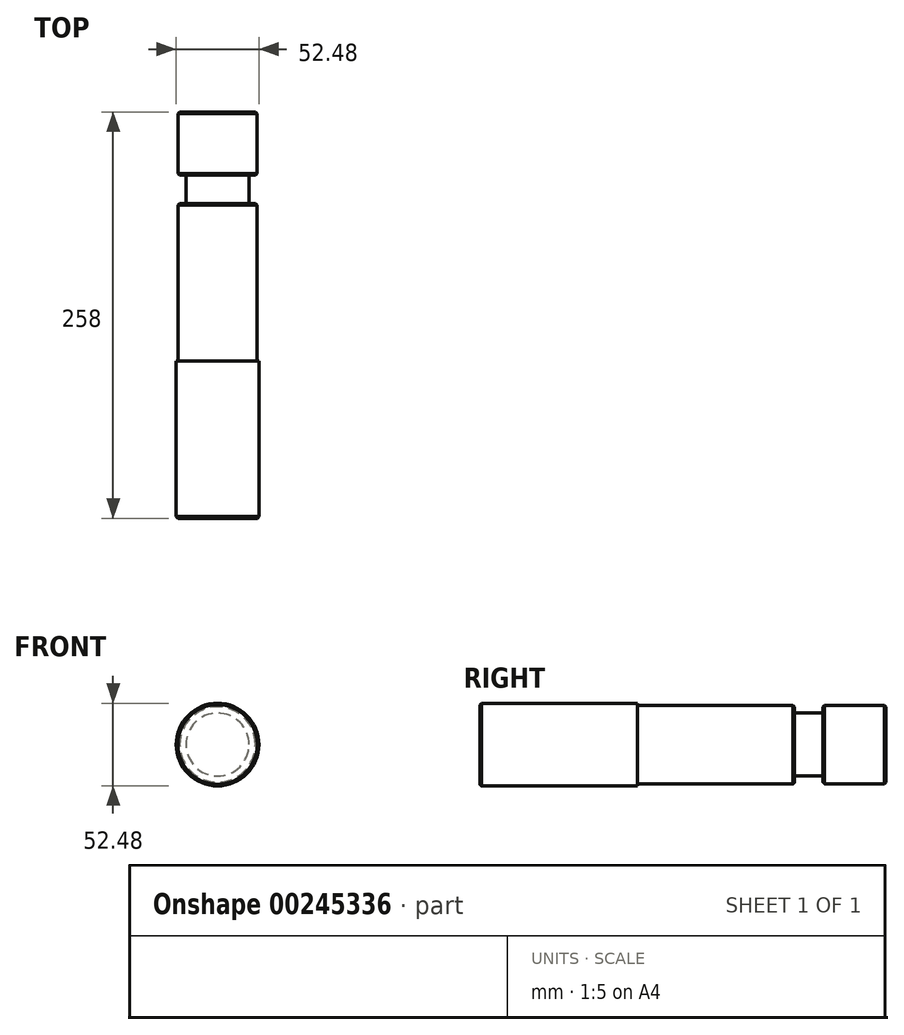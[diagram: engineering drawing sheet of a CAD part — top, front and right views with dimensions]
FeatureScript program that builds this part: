
annotation { "Feature Type Name" : "Feature", "Feature Type Description" : "" }
export const myFeature = defineFeature(function(context is Context, id is Id, definition is map)
    precondition{}
    {
        {
            var Q0;
            Q0=qCreatedBy(makeId("Front.planeOp"),FACE);
            var sketch = newSketch(context, id + "F0", { "sketchPlane" : qUnion([Q0])});
            skCircle(sketch, "E0", {"center": v(0, 0) * mm, "radius": 25 * mm});
            skSolve(sketch);
        }
        {
            var Q0;
            Q0 = qSketchRegion(id + "F0", true);
            extrude(context, id + "F1", {"entities" : qUnion([Q0]), "depth" : 40 * mm});
        }
        {
            var Q0;
            Q0=makeQuery(id+"F1.opExtrude","CAP_FACE",FACE,{"disambiguationData":[OSD([sQuery(id+"F0.wireOp",EDGE,"E0")])],"isStart":false});
            var sketch = newSketch(context, id + "F2", { "sketchPlane" : qUnion([Q0])});
            skCircle(sketch, "E1", {"center": v(0, 0) * mm, "radius": 20 * mm});
            skSolve(sketch);
        }
        {
            var Q0;
            Q0 = qSketchRegion(id + "F2", true);
            extrude(context, id + "F3", {"entities" : qUnion([Q0]), "operationType" : NewBodyOperationType.ADD, "depth" : 18 * mm});
        }
        {
            var Q0;
            Q0=makeQuery(id+"FrGzE71CMQSHOiY_1.opExtrude","CAP_EDGE",EDGE,{"disambiguationData":[OSD([sQuery(id+"FCd7hvli7ik8MWt_1.wireOp",EDGE,"2UGgOSmH-1Rk6-lXhe-eLAG-fFupfOh3HAAi")])],"isStart":true});
            var Q1;
            Q1=makeQuery(id+"F1.opExtrude","CAP_EDGE",EDGE,{"disambiguationData":[OSD([sQuery(id+"F0.wireOp",EDGE,"E0")])],"isStart":false});
            var Q2;
            Q2=makeQuery(id+"F1.opExtrude","CAP_EDGE",EDGE,{"disambiguationData":[OSD([sQuery(id+"F0.wireOp",EDGE,"E0")])],"isStart":true});
            chamfer(context, id + "F4", {"entities" : qUnion([Q0, Q1, Q2]), "width" : 1 * mm, "tangentPropagation" : true});
        }
        {
            var Q0;
            Q0=makeQuery(id+"F3.opExtrude","CAP_FACE",FACE,{"disambiguationData":[OSD([sQuery(id+"F2.wireOp",EDGE,"E1")])],"isStart":false});
            var sketch = newSketch(context, id + "F5", { "sketchPlane" : qUnion([Q0])});
            skCircle(sketch, "E2", {"center": v(0, 0) * mm, "radius": 25 * mm});
            skSolve(sketch);
        }
        {
            var Q0;
            Q0 = qSketchRegion(id + "F5", true);
            extrude(context, id + "F6", {"entities" : qUnion([Q0]), "operationType" : NewBodyOperationType.ADD, "offsetDistance" : 25 * mm, "depth" : 100 * mm});
        }
        {
            var Q0;
            Q0=makeQuery(id+"F6.opExtrude","CAP_EDGE",EDGE,{"disambiguationData":[OSD([sQuery(id+"F5.wireOp",EDGE,"E2")])],"isStart":true});
            chamfer(context, id + "F7", {"entities" : qUnion([Q0]), "width" : 1 * mm, "tangentPropagation" : true});
        }
        {
            var Q0;
            Q0=makeQuery(id+"F6.opExtrude","CAP_FACE",FACE,{"disambiguationData":[OSD([sQuery(id+"F5.wireOp",EDGE,"E2")])],"isStart":false});
            var sketch = newSketch(context, id + "F8", { "sketchPlane" : qUnion([Q0])});
            skCircle(sketch, "E3", {"center": v(0, 0) * mm, "radius": 26.24 * mm});
            skSolve(sketch);
        }
        {
            var Q0;
            Q0 = qSketchRegion(id + "F8", true);
            extrude(context, id + "F9", {"entities" : qUnion([Q0]), "operationType" : NewBodyOperationType.ADD, "depth" : 100 * mm});
        }
        {
            var Q0;
            Q0=makeQuery(id+"F9.opExtrude","CAP_EDGE",EDGE,{"disambiguationData":[OSD([sQuery(id+"F8.wireOp",EDGE,"E3")])],"isStart":false});
            chamfer(context, id + "F10", {"entities" : qUnion([Q0]), "width" : 1 * mm, "tangentPropagation" : true});
        }
    });
